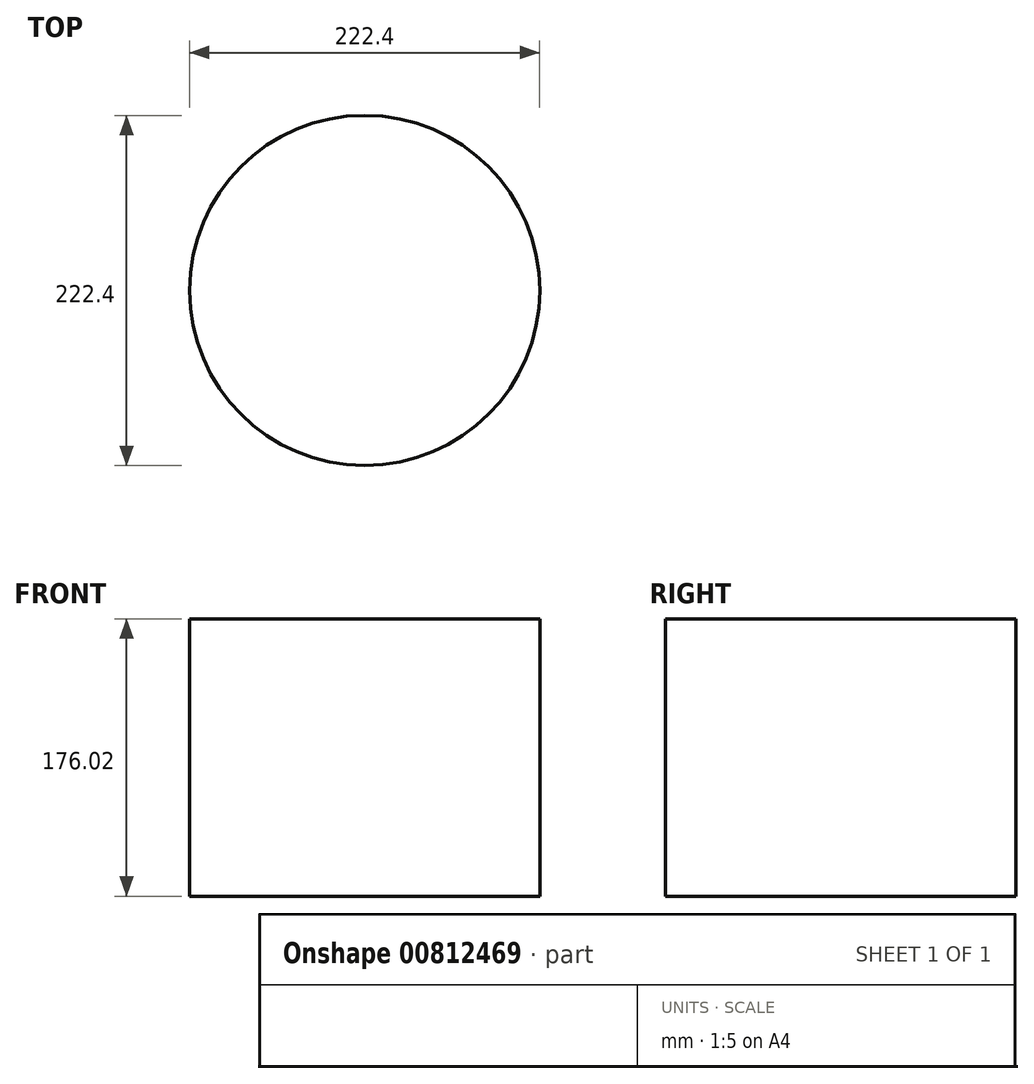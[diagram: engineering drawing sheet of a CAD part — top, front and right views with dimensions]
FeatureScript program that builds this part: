
annotation { "Feature Type Name" : "Feature", "Feature Type Description" : "" }
export const myFeature = defineFeature(function(context is Context, id is Id, definition is map)
    precondition{}
    {
        {
            var Q0;
            Q0=qCreatedBy(makeId("Top.planeOp"),FACE);
            var sketch = newSketch(context, id + "F0", { "sketchPlane" : qUnion([Q0])});
            skCircle(sketch, "E0", {"center": v(0, -84.7) * mm, "radius": 111.2 * mm});
            skSolve(sketch);
        }
        {
            var Q0;
            Q0=makeQuery(id+"F0.imprint","IMPRINT",FACE,{"disambiguationData":[TD([[makeQuery(id+"F0.imprint","IMPRINT",EDGE,{"derivedFrom":sQuery(id+"F0.wireOp",EDGE,"E0")}),1.0]])]});
            extrude(context, id + "F1", {"entities" : qUnion([Q0]), "depth" : 176.02 * mm, "offsetDistance" : 25.4 * mm});
        }
    });
